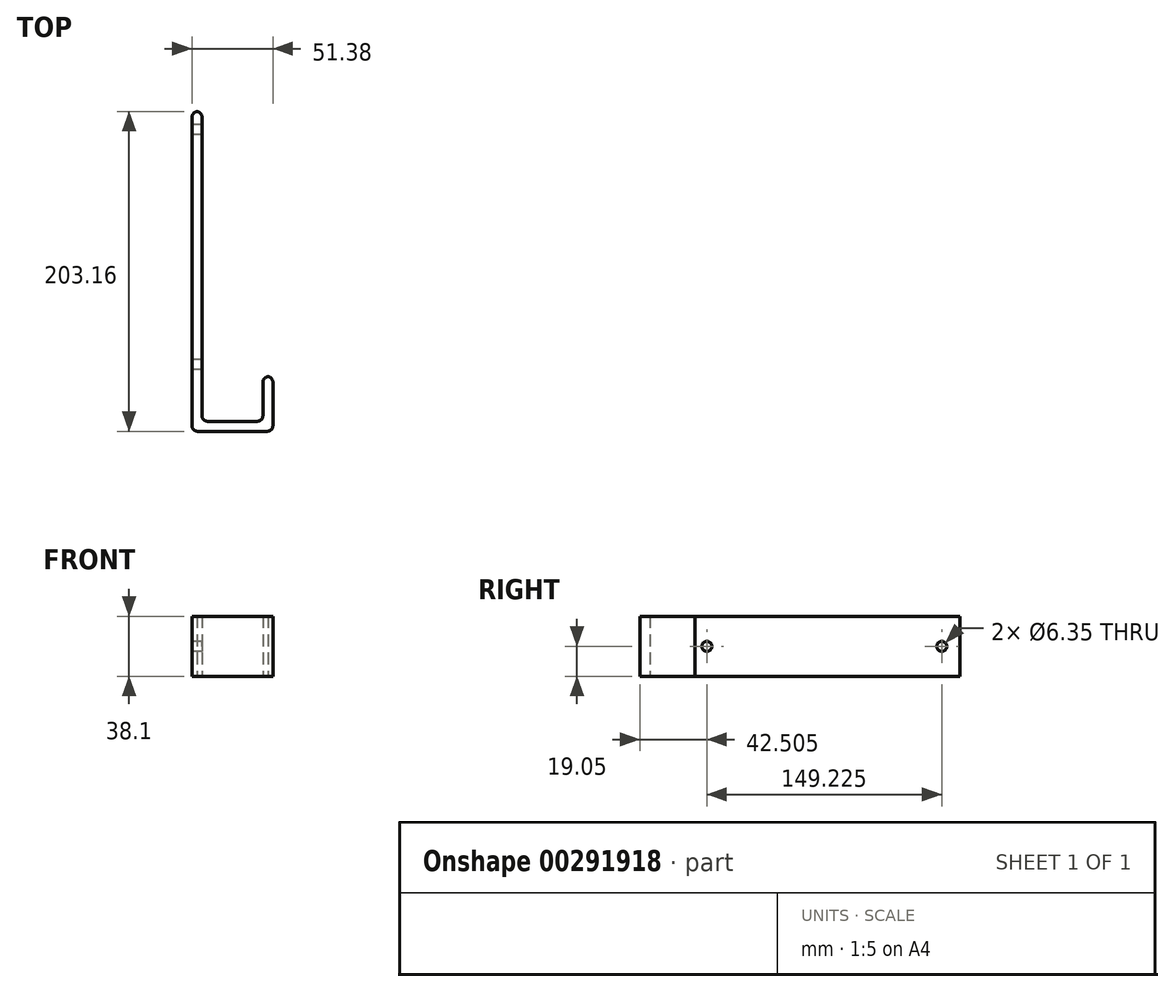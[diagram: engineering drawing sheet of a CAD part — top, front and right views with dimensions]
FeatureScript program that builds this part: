
annotation { "Feature Type Name" : "Feature", "Feature Type Description" : "" }
export const myFeature = defineFeature(function(context is Context, id is Id, definition is map)
    precondition{}
    {
        {
            var Q0;
            Q0=qCreatedBy(makeId("Top.planeOp"),FACE);
            var sketch = newSketch(context, id + "F0", { "sketchPlane" : qUnion([Q0])});
            skLineSegment(sketch, "E0.bottom", {"start": v(-17.24, 145.49) * mm, "end": v(-10.9, 145.49) * mm});
            skLineSegment(sketch, "E0.top", {"start": v(-17.24, -57.71) * mm, "end": v(-10.9, -57.71) * mm});
            skLineSegment(sketch, "E0.left", {"start": v(-17.24, 145.49) * mm, "end": v(-17.24, -57.71) * mm});
            skLineSegment(sketch, "E0.right", {"start": v(-10.9, 145.49) * mm, "end": v(-10.9, -57.71) * mm});
            skLineSegment(sketch, "E1.bottom", {"start": v(-10.9, -51.36) * mm, "end": v(27.8, -51.36) * mm});
            skLineSegment(sketch, "E1.top", {"start": v(-10.9, -57.71) * mm, "end": v(27.8, -57.71) * mm});
            skLineSegment(sketch, "E1.left", {"start": v(-10.9, -51.36) * mm, "end": v(-10.9, -57.71) * mm});
            skLineSegment(sketch, "E1.right", {"start": v(27.8, -51.36) * mm, "end": v(27.8, -57.71) * mm});
            skLineSegment(sketch, "E2.bottom", {"start": v(27.8, -57.71) * mm, "end": v(34.14, -57.71) * mm});
            skLineSegment(sketch, "E2.top", {"start": v(27.8, -22.86) * mm, "end": v(34.14, -22.86) * mm});
            skLineSegment(sketch, "E2.left", {"start": v(27.8, -57.71) * mm, "end": v(27.8, -22.86) * mm});
            skLineSegment(sketch, "E2.right", {"start": v(34.14, -57.71) * mm, "end": v(34.14, -22.86) * mm});
            skSolve(sketch);
        }
        {
            var Q0;
            Q0 = qSketchRegion(id + "F0", true);
            extrude(context, id + "F1", {"entities" : qUnion([Q0]), "depth" : 38.1 * mm});
        }
        {
            var Q0;
            Q0=makeQuery(id+"F1.opExtrude","SWEPT_EDGE",EDGE,{"disambiguationData":[OSD([sQuery(id+"F0.wireOp",EDGE,"E0.right"),sQuery(id+"F0.wireOp",EDGE,"E1.bottom"),sQuery(id+"F0.wireOp",EDGE,"E1.left")])]});
            var Q1;
            Q1=makeQuery(id+"F1.opExtrude","SWEPT_EDGE",EDGE,{"disambiguationData":[OSD([sQuery(id+"F0.wireOp",EDGE,"E1.bottom"),sQuery(id+"F0.wireOp",EDGE,"E2.left")])]});
            var Q2;
            Q2=makeQuery(id+"F1.opExtrude","SWEPT_EDGE",EDGE,{"disambiguationData":[OSD([sQuery(id+"F0.wireOp",EDGE,"E2.top"),sQuery(id+"F0.wireOp",EDGE,"E2.left")])]});
            var Q3;
            Q3=makeQuery(id+"F1.opExtrude","SWEPT_EDGE",EDGE,{"disambiguationData":[OSD([sQuery(id+"F0.wireOp",EDGE,"E2.top"),sQuery(id+"F0.wireOp",EDGE,"E2.right")])]});
            var Q4;
            Q4=makeQuery(id+"F1.opExtrude","SWEPT_EDGE",EDGE,{"disambiguationData":[OSD([sQuery(id+"F0.wireOp",EDGE,"E0.top"),sQuery(id+"F0.wireOp",EDGE,"E0.left")])]});
            var Q5;
            Q5=makeQuery(id+"F1.opExtrude","SWEPT_EDGE",EDGE,{"disambiguationData":[OSD([sQuery(id+"F0.wireOp",EDGE,"E2.bottom"),sQuery(id+"F0.wireOp",EDGE,"E2.right")])]});
            var Q6;
            Q6=makeQuery(id+"F1.opExtrude","SWEPT_EDGE",EDGE,{"disambiguationData":[OSD([sQuery(id+"F0.wireOp",EDGE,"E0.bottom"),sQuery(id+"F0.wireOp",EDGE,"E0.right")])]});
            var Q7;
            Q7=makeQuery(id+"F1.opExtrude","SWEPT_EDGE",EDGE,{"disambiguationData":[OSD([sQuery(id+"F0.wireOp",EDGE,"E0.bottom"),sQuery(id+"F0.wireOp",EDGE,"E0.left")])]});
            fillet(context, id + "F2", {"entities" : qUnion([Q0, Q1, Q2, Q3, Q4, Q5, Q6, Q7]), "radius" : 3.68 * mm, "tangentPropagation" : true, "allowEdgeOverflow" : false});
        }
        {
            var Q0;
            Q0=makeQuery(id+"F1.opExtrude","SWEPT_FACE",FACE,{"disambiguationData":[OSD([sQuery(id+"F0.wireOp",EDGE,"E0.left")])]});
            var sketch = newSketch(context, id + "F3", { "sketchPlane" : qUnion([Q0])});
            skCircle(sketch, "E3", {"center": v(-134.02, 19.05) * mm, "radius": 3.18 * mm});
            skCircle(sketch, "E4", {"center": v(15.2, 19.05) * mm, "radius": 3.18 * mm});
            skSolve(sketch);
        }
        {
            var Q0;
            Q0 = qSketchRegion(id + "F3", true);
            extrude(context, id + "F4", {"entities" : qUnion([Q0]), "operationType" : NewBodyOperationType.REMOVE, "oppositeDirection" : true, "depth" : 25.4 * mm});
        }
    });
